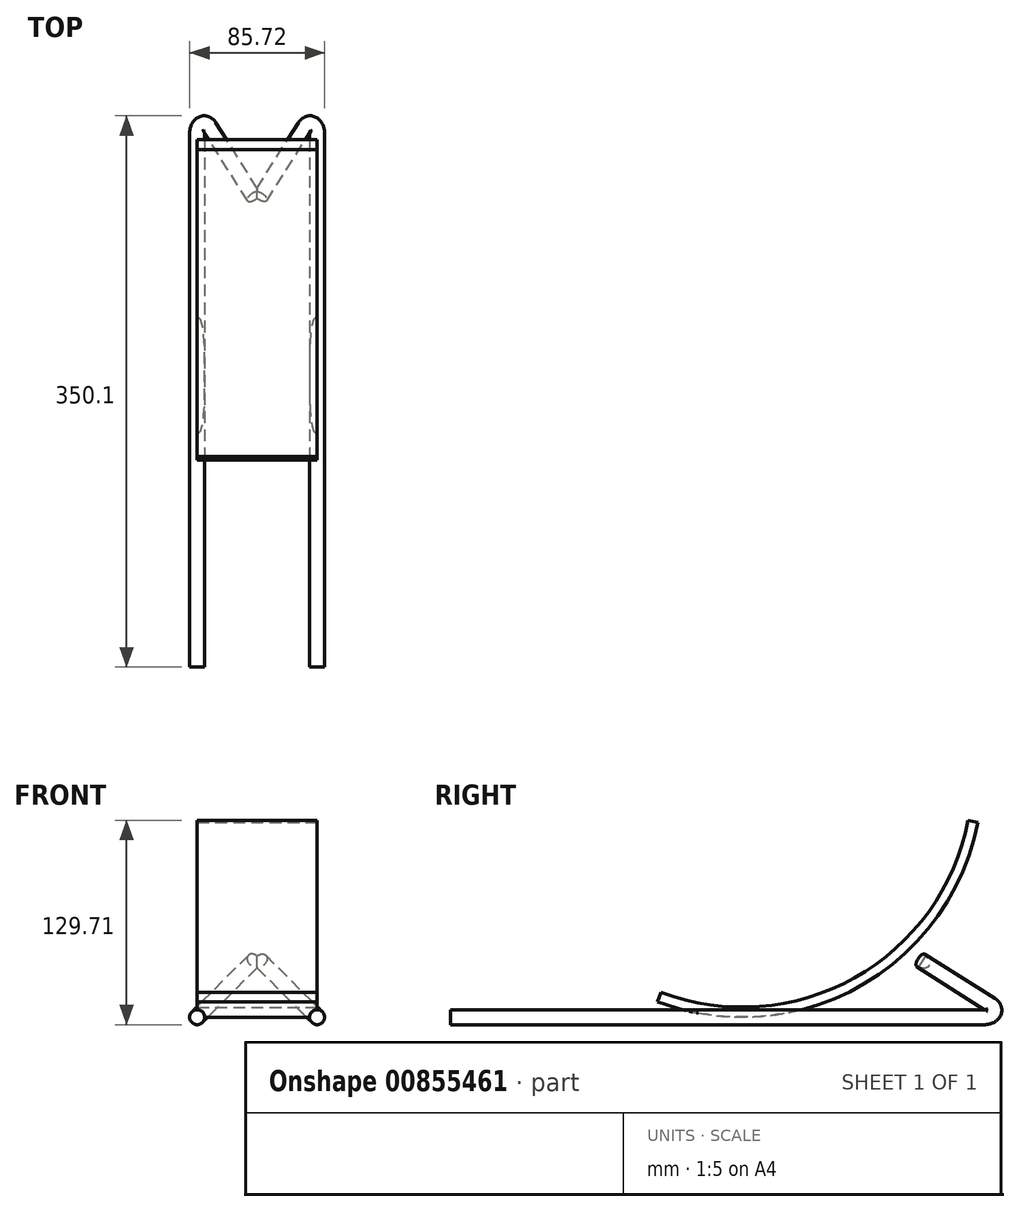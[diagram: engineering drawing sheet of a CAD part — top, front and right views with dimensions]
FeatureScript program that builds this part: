
annotation { "Feature Type Name" : "Feature", "Feature Type Description" : "" }
export const myFeature = defineFeature(function(context is Context, id is Id, definition is map)
    precondition{}
    {
        {
            var Q0;
            Q0=qCreatedBy(makeId("Right.planeOp"),FACE);
            var sketch = newSketch(context, id + "F0", { "sketchPlane" : qUnion([Q0])});
            skLineSegment(sketch, "E0", {"start": v(-236.4, 0) * mm, "end": v(102.58, 0) * mm});
            skLineSegment(sketch, "E1", {"start": v(106.82, 11.08) * mm, "end": v(62.42, 50.81) * mm});
            skPoint(sketch, "E2.visualSharp", {"position": v(119.2, 0) * mm});
            skArc(sketch, "E2.filletArc", {"start": v(102.58, 0) * mm, "mid": v(108.52, 4.08) * mm, "end": v(106.82, 11.08) * mm});
            skSolve(sketch);
        }
        {
            var Q0;
            Q0=qCreatedBy(makeId("Front.planeOp"),FACE);
            var sketch = newSketch(context, id + "F1", { "sketchPlane" : qUnion([Q0])});
            skCircle(sketch, "E3", {"center": v(0, 0) * mm, "radius": 4.76 * mm});
            skSolve(sketch);
        }
        {
            var Q0;
            Q0=makeQuery(id+"F1.imprint","IMPRINT",FACE,{"disambiguationData":[TD([[makeQuery(id+"F1.imprint","IMPRINT",EDGE,{"derivedFrom":sQuery(id+"F1.wireOp",EDGE,"E3")}),1.0]])]});
            var Q1;
            Q1=sQuery(id+"F0.wireOp",EDGE,"E0");
            var Q2;
            Q2=sQuery(id+"F0.wireOp",EDGE,"E2.filletArc");
            var Q3;
            Q3=sQuery(id+"F0.wireOp",EDGE,"E1");
            sweep(context, id + "F2", {"profiles" : qUnion([Q0]), "path" : qUnion([Q1, Q2, Q3])});
        }
        {
            var Q0;
            Q0=qCreatedBy(makeId("Right.planeOp"),FACE);
            var sketch = newSketch(context, id + "F3", { "sketchPlane" : qUnion([Q0])});
            skLineSegment(sketch, "E4.0", {"start": v(65.6, 54.36) * mm, "end": v(59.24, 47.26) * mm});
            skLineSegment(sketch, "E5", {"start": v(62.42, 50.81) * mm, "end": v(-51.15, 152.43) * mm, "construction": true});
            skArc(sketch, "E6", {"start": v(62.42, 50.81) * mm, "mid": v(85.43, 84.83) * mm, "end": v(98.52, 123.75) * mm});
            skArc(sketch, "E7", {"start": v(62.42, 50.81) * mm, "mid": v(-14.9, 4.4) * mm, "end": v(-104.92, 9.83) * mm});
            skArc(sketch, "E8.0", {"start": v(57.69, 55.05) * mm, "mid": v(-16.41, 10.58) * mm, "end": v(-102.68, 15.77) * mm});
            skArc(sketch, "E8.1", {"start": v(57.69, 55.05) * mm, "mid": v(79.74, 87.64) * mm, "end": v(92.29, 124.95) * mm});
            skLineSegment(sketch, "E9", {"start": v(-102.68, 15.77) * mm, "end": v(-104.92, 9.83) * mm});
            skLineSegment(sketch, "E10", {"start": v(92.29, 124.95) * mm, "end": v(98.52, 123.75) * mm});
            skSolve(sketch);
        }
        {
            var Q0;
            Q0=makeQuery(id+"F2.opSweep","SWEPT_BODY",BODY,{"disambiguationData":[OSD([sQuery(id+"F0.wireOp",EDGE,"E1"),sQuery(id+"F1.wireOp",EDGE,"E3")])]});
            var Q1;
            Q1=sQuery(id+"F0.wireOp",EDGE,"E0");
            transform(context, id + "F4", {"entities" : qUnion([Q0]), "transformType" : TransformType.ROTATION, "transformAxis" : qUnion([Q1]), "angle" : 45 * degree, "oppositeDirection" : true, "makeCopy" : false});
        }
        {
            var Q0;
            Q0=makeQuery(id+"F3.imprint","IMPRINT",FACE,{"disambiguationData":[TD([[makeQuery(id+"F3.imprint","IMPRINT",EDGE,{"derivedFrom":sQuery(id+"F3.wireOp",EDGE,"E6")}),1.0]])]});
            extrude(context, id + "F5", {"entities" : qUnion([Q0]), "oppositeDirection" : true, "depth" : 38.1 * mm, "offsetDistance" : 25.4 * mm});
        }
        {
            var Q0;
            Q0=makeQuery(id+"F2.opSweep","SWEPT_BODY",BODY,{"disambiguationData":[OSD([sQuery(id+"F0.wireOp",EDGE,"E1"),sQuery(id+"F1.wireOp",EDGE,"E3")])]});
            var Q1;
            Q1=makeQuery(id+"F5.opExtrude","CAP_FACE",FACE,{"disambiguationData":[OSD([sQuery(id+"F3.wireOp",EDGE,"E6"),sQuery(id+"F3.wireOp",EDGE,"E7"),sQuery(id+"F3.wireOp",EDGE,"E8.0"),sQuery(id+"F3.wireOp",EDGE,"E8.1"),sQuery(id+"F3.wireOp",EDGE,"E9"),sQuery(id+"F3.wireOp",EDGE,"E10")])],"isStart":false});
            mirror(context, id + "F6", {"entities" : qUnion([Q0]), "mirrorPlane" : qUnion([Q1])});
        }
        {
            var Q0;
            Q0=makeQuery(id+"F5.opExtrude","SWEPT_BODY",BODY,{"disambiguationData":[OSD([sQuery(id+"F3.wireOp",EDGE,"E6"),sQuery(id+"F3.wireOp",EDGE,"E7"),sQuery(id+"F3.wireOp",EDGE,"E8.0"),sQuery(id+"F3.wireOp",EDGE,"E8.1"),sQuery(id+"F3.wireOp",EDGE,"E9"),sQuery(id+"F3.wireOp",EDGE,"E10")])]});
            var Q1;
            Q1=makeQuery(id+"F5.opExtrude","CAP_FACE",FACE,{"disambiguationData":[OSD([sQuery(id+"F3.wireOp",EDGE,"E6"),sQuery(id+"F3.wireOp",EDGE,"E7"),sQuery(id+"F3.wireOp",EDGE,"E8.0"),sQuery(id+"F3.wireOp",EDGE,"E8.1"),sQuery(id+"F3.wireOp",EDGE,"E9"),sQuery(id+"F3.wireOp",EDGE,"E10")])],"isStart":false});
            mirror(context, id + "F7", {"operationType" : NewBodyOperationType.ADD, "entities" : qUnion([Q0]), "mirrorPlane" : qUnion([Q1])});
        }
    });
